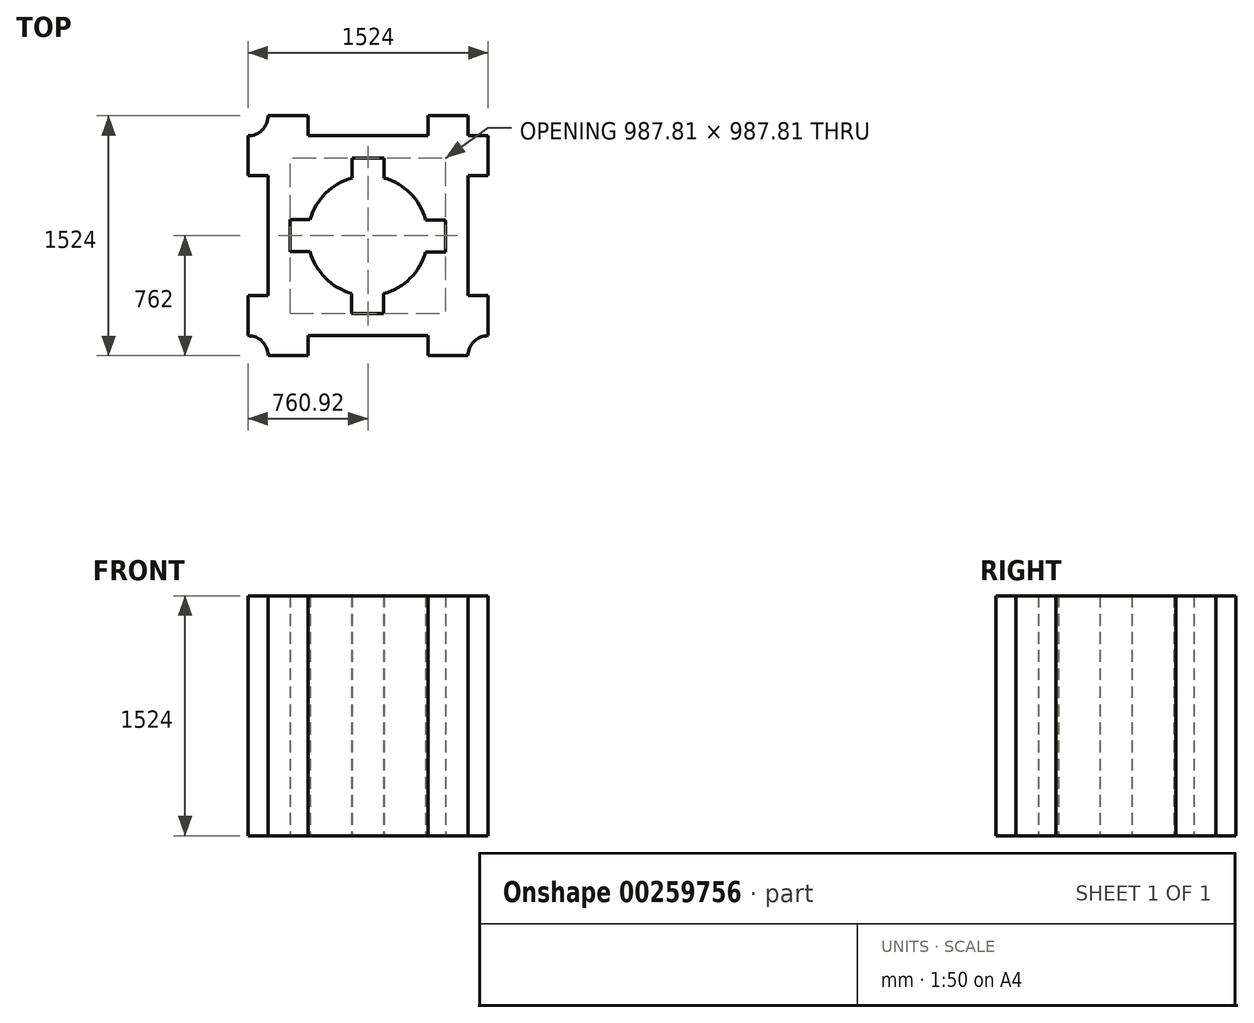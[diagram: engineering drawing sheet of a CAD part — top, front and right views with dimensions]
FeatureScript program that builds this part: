
annotation { "Feature Type Name" : "Feature", "Feature Type Description" : "" }
export const myFeature = defineFeature(function(context is Context, id is Id, definition is map)
    precondition{}
    {
        {
            var Q0;
            Q0=qCreatedBy(makeId("Top.planeOp"),FACE);
            var sketch = newSketch(context, id + "F0", { "sketchPlane" : qUnion([Q0])});
            skLineSegment(sketch, "E0", {"start": v(0, 0) * mm, "end": v(0, -254) * mm});
            skLineSegment(sketch, "E1", {"start": v(0, -254) * mm, "end": v(127, -254) * mm});
            skLineSegment(sketch, "E2", {"start": v(0, 127) * mm, "end": v(127, 127) * mm});
            skArc(sketch, "E3", {"start": v(0, 0) * mm, "mid": v(89.8, 37.2) * mm, "end": v(127, 127) * mm});
            skLineSegment(sketch, "E4", {"start": v(127, 127) * mm, "end": v(381, 127) * mm});
            skLineSegment(sketch, "E5", {"start": v(381, 127) * mm, "end": v(381, 0) * mm});
            skLineSegment(sketch, "E6", {"start": v(381, 0) * mm, "end": v(1143, 0) * mm});
            skLineSegment(sketch, "E7", {"start": v(1143, 0) * mm, "end": v(1143, 127) * mm});
            skLineSegment(sketch, "E8", {"start": v(1143, 127) * mm, "end": v(1397, 127) * mm});
            skLineSegment(sketch, "E9", {"start": v(1397, 127) * mm, "end": v(1397, 0) * mm});
            skLineSegment(sketch, "E10", {"start": v(1397, 0) * mm, "end": v(1524, 0) * mm});
            skArc(sketch, "E11", {"start": v(1397, 127) * mm, "mid": v(1434.2, 37.2) * mm, "end": v(1524, 0) * mm});
            skLineSegment(sketch, "E12", {"start": v(1524, 0) * mm, "end": v(1524, -254) * mm});
            skLineSegment(sketch, "E13", {"start": v(1524, -254) * mm, "end": v(1397, -254) * mm});
            skLineSegment(sketch, "E14", {"start": v(127, -254) * mm, "end": v(127, -635) * mm});
            skLineSegment(sketch, "E15", {"start": v(1397, -254) * mm, "end": v(1397, -635) * mm});
            skLineSegment(sketch, "E16.MirrorCS", {"start": v(127, -1016) * mm, "end": v(127, -635) * mm});
            skLineSegment(sketch, "E17.MirrorCS", {"start": v(0, -1016) * mm, "end": v(127, -1016) * mm});
            skLineSegment(sketch, "E18.MirrorCS", {"start": v(0, -1270) * mm, "end": v(0, -1016) * mm});
            skArc(sketch, "E19.MirrorCS", {"start": v(0, -1270) * mm, "mid": v(89.8, -1307.2) * mm, "end": v(127, -1397) * mm});
            skLineSegment(sketch, "E20.MirrorCS", {"start": v(127, -1397) * mm, "end": v(381, -1397) * mm});
            skLineSegment(sketch, "E21.MirrorCS", {"start": v(381, -1397) * mm, "end": v(381, -1270) * mm});
            skLineSegment(sketch, "E22.MirrorCS", {"start": v(381, -1270) * mm, "end": v(1143, -1270) * mm});
            skLineSegment(sketch, "E23.MirrorCS", {"start": v(1143, -1270) * mm, "end": v(1143, -1397) * mm});
            skLineSegment(sketch, "E24.MirrorCS", {"start": v(1143, -1397) * mm, "end": v(1397, -1397) * mm});
            skArc(sketch, "E25.MirrorCS", {"start": v(1397, -1397) * mm, "mid": v(1434.2, -1307.2) * mm, "end": v(1524, -1270) * mm});
            skLineSegment(sketch, "E26.MirrorCS", {"start": v(1524, -1270) * mm, "end": v(1524, -1016) * mm});
            skLineSegment(sketch, "E27.MirrorCS", {"start": v(1524, -1016) * mm, "end": v(1397, -1016) * mm});
            skLineSegment(sketch, "E28.MirrorCS", {"start": v(1397, -1016) * mm, "end": v(1397, -635) * mm});
            skLineSegment(sketch, "E29", {"start": v(127, -635) * mm, "end": v(760.92, -635) * mm});
            skArc(sketch, "E30", {"start": v(393.42, -735.52) * mm, "mid": v(490.72, -903.61) * mm, "end": v(658.24, -1001.9) * mm});
            skLineSegment(sketch, "E31.bottom", {"start": v(660.4, -141.1) * mm, "end": v(863.6, -141.1) * mm});
            skLineSegment(sketch, "E31.left", {"start": v(660.4, -141.1) * mm, "end": v(660.4, -268.1) * mm});
            skLineSegment(sketch, "E31.right", {"start": v(863.6, -141.1) * mm, "end": v(863.6, -268.1) * mm});
            skLineSegment(sketch, "E32", {"start": v(762, -141.1) * mm, "end": v(762, -78.34) * mm});
            skLineSegment(sketch, "E33.1.0", {"start": v(267.02, -735.52) * mm, "end": v(267.02, -532.32) * mm});
            skLineSegment(sketch, "E33.1.1", {"start": v(267.02, -735.52) * mm, "end": v(394.02, -735.52) * mm});
            skLineSegment(sketch, "E33.1.3", {"start": v(267.02, -532.32) * mm, "end": v(394.02, -532.32) * mm});
            skLineSegment(sketch, "E33.2.0", {"start": v(861.44, -1128.9) * mm, "end": v(658.24, -1128.9) * mm});
            skLineSegment(sketch, "E33.2.1", {"start": v(861.44, -1128.9) * mm, "end": v(861.44, -1001.9) * mm});
            skLineSegment(sketch, "E33.2.3", {"start": v(658.24, -1128.9) * mm, "end": v(658.24, -1001.9) * mm});
            skLineSegment(sketch, "E33.3.0", {"start": v(1254.82, -534.48) * mm, "end": v(1254.82, -737.68) * mm});
            skLineSegment(sketch, "E33.3.1", {"start": v(1254.82, -534.48) * mm, "end": v(1127.82, -534.48) * mm});
            skLineSegment(sketch, "E33.3.3", {"start": v(1254.82, -737.68) * mm, "end": v(1127.82, -737.68) * mm});
            skArc(sketch, "E34.trimOffspring", {"start": v(660.4, -267.5) * mm, "mid": v(492.3, -364.8) * mm, "end": v(394.02, -532.32) * mm});
            skArc(sketch, "E35.trimOffspring", {"start": v(1128.42, -534.48) * mm, "mid": v(1031.12, -366.39) * mm, "end": v(863.6, -268.1) * mm});
            skArc(sketch, "E36.trimOffspring", {"start": v(861.44, -1002.5) * mm, "mid": v(1029.53, -905.2) * mm, "end": v(1127.82, -737.68) * mm});
            skSolve(sketch);
        }
        {
            var Q0;
            Q0=makeQuery(id+"F0.imprint","IMPRINT",FACE,{"disambiguationData":[TD([[makeQuery(id+"F0.imprint","IMPRINT",EDGE,{"derivedFrom":sQuery(id+"F0.wireOp",EDGE,"E0")}),1.0]])]});
            extrude(context, id + "F1", {"entities" : qUnion([Q0]), "depth" : 1524 * mm});
        }
    });
